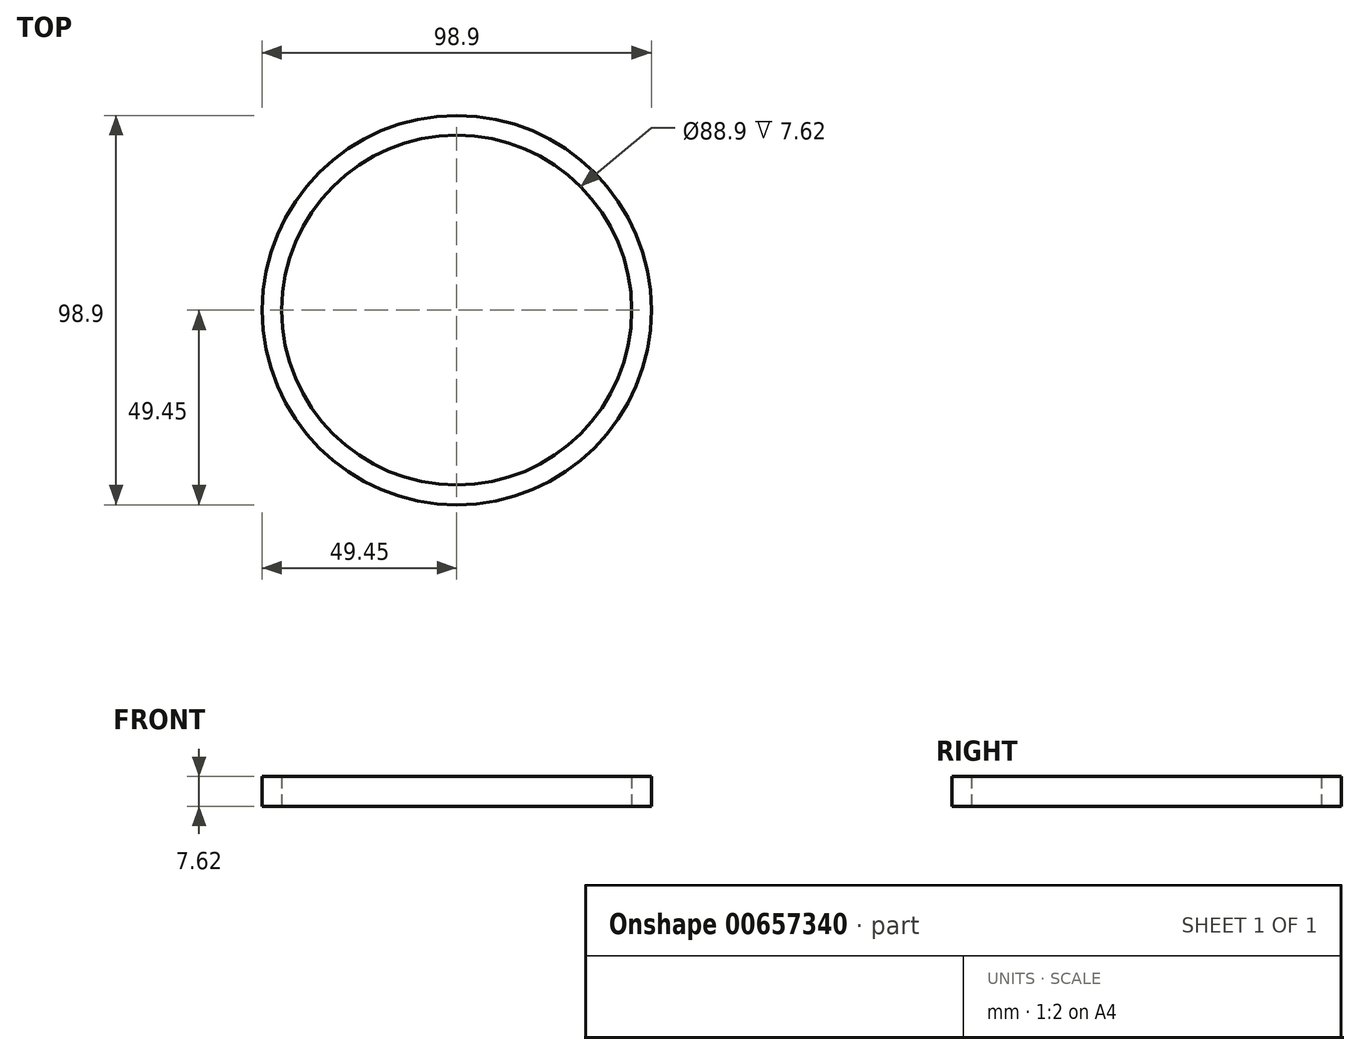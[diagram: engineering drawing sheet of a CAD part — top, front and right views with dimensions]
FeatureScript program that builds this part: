
annotation { "Feature Type Name" : "Feature", "Feature Type Description" : "" }
export const myFeature = defineFeature(function(context is Context, id is Id, definition is map)
    precondition{}
    {
        {
            var Q0;
            Q0=qCreatedBy(makeId("Top.planeOp"),FACE);
            var sketch = newSketch(context, id + "F0", { "sketchPlane" : qUnion([Q0])});
            skCircle(sketch, "E0", {"center": v(0, 0) * mm, "radius": 49.45 * mm});
            skCircle(sketch, "E1", {"center": v(0, 0) * mm, "radius": 44.45 * mm});
            skSolve(sketch);
        }
        {
            var Q0;
            Q0=makeQuery(id+"F0.imprint","IMPRINT",FACE,{"disambiguationData":[TD([[makeQuery(id+"F0.imprint","IMPRINT",EDGE,{"derivedFrom":sQuery(id+"F0.wireOp",EDGE,"E0")}),1.0]])]});
            extrude(context, id + "F1", {"entities" : qUnion([Q0]), "depth" : 7.62 * mm, "offsetDistance" : 25 * mm});
        }
    });
